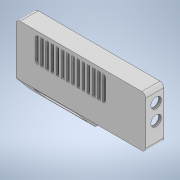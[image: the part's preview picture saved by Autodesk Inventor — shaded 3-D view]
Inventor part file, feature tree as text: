
AUTODESK INVENTOR PART (.ipt)
format: ipt  version: 2021 (Build 250183000, 183)  size: 544,768 bytes
history: native  units: mm
features: sketch x22, extrude x21, chamfer x6, fillet x4, hole x1
ambient origin geometry x8: Origin, YZ Plane, XZ Plane, XY Plane, X Axis, Y Axis, Z Axis, Center Point
bodies: Solid1 (feature_tree)
feature tree (54):
  extrude  "Extrusion1"  Depth=100.0mm
  extrude  "Extrusion3"  Depth=50.0mm
  extrude  "Extrusion4"  Depth=12.5mm
  extrude  "Extrusion12"  Depth=3.0mm TaperAngle=0.0deg
  extrude  "Extrusion13"  Depth=3.0mm TaperAngle=0.0deg
  fillet  "Fillet3"  Radius=2.0mm
  extrude  "Extrusion15"  Depth=2.0mm
  extrude  "Extrusion20"  Depth=1.2mm
  extrude  "Extrusion21"  Depth=12.0mm TaperAngle=0.0deg
  extrude  "Extrusion22"  Depth=2.0mm
  extrude  "Extrusion23"  Depth=3.0mm
  extrude  "Extrusion26"  Depth=4.4mm TaperAngle=0.0deg
  hole  "Hole2"  [1 undecoded]
  chamfer  "Chamfer3"  Distance=12.0mm
  chamfer  "Chamfer4"  Distance=12.0mm
  chamfer  "Chamfer5"  Distance=2.0mm
  chamfer  "Chamfer6"  Distance=2.0mm
  chamfer  "Chamfer7"  Distance=3.0mm
  extrude  "Extrusion27"  Depth=3.0mm
  fillet  "Fillet4"  Radius=3.0mm
  extrude  "Extrusion28"  Depth=50.0mm
  extrude  "Extrusion29"  Depth=0.5mm
  extrude  "Extrusion30"  Depth=15.0mm
  fillet  "Fillet5"  Radius=3.0mm
  extrude  "Extrusion34"  Depth=3.0mm
  extrude  "Extrusion35"  Depth=0.5mm
  extrude  "Extrusion36"  Depth=0.5mm
  extrude  "Extrusion37"  Depth=0.5mm
  fillet  "Fillet6"  Radius=4.8mm
  extrude  "Extrusion38"  Depth=0.5mm
  extrude  "Extrusion39"  Depth=0.5mm
  chamfer  "Chamfer8"  Distance=4.8mm
  sketch  "Sketch1"  dims[d0=52.0mm d1=100.0mm]
  sketch  "Sketch4"  dims[d2=26.0mm d3=50.0mm]
  sketch  "Sketch5"  dims[d4=2.0mm d5=0.0mm d35=12.5mm]
  sketch  "Sketch13"  dims[d36=63.1mm d37=3.0mm d38=0.0mm]
  sketch  "Sketch14"  dims[d39=50.673mm d40=3.0mm d41=0.0mm d79=2.0mm]
  sketch  "Sketch16"  dims[d80=2.0mm d81=2.0mm]
  sketch  "Sketch21"  dims[d82=1.2mm d83=44.0mm]
  sketch  "Sketch22"  dims[d84=59.0mm d85=12.0mm d86=0.0mm]
  sketch  "Sketch23"  dims[d87=2.0mm d88=12.6mm]
  sketch  "Sketch24"  dims[d89=12.0mm d90=0.0mm d91=3.0mm]
  sketch  "Sketch27"  dims[d95=33.8mm d96=4.4mm d97=0.0mm]
  sketch  "Sketch28"  dims[d117=2.0mm d118=2.0mm d119=12.0mm d120=0.0mm d121=12.0mm d122=0.0mm]
  sketch  "Sketch29"  dims[d123=70.0mm]
  sketch  "Sketch30"  dims[d124=89.0mm]
  sketch  "Sketch31"  dims[d125=8.0mm]
  sketch  "Sketch32"  dims[d126=8.0mm d127=2.0mm d128=0.0mm]
  sketch  "Sketch36"  dims[d129=8.0mm]
  sketch  "Sketch37"  dims[d130=10.0mm]
  sketch  "Sketch38"  dims[d131=12.0mm]
  sketch  "Sketch39"  dims[d132=8.0mm]
  sketch  "Sketch40"  dims[d133=8.0mm]
  sketch  "Sketch41"  dims[d134=8.0mm d135=2.0mm d136=0.0mm d144=3.0mm d145=3.0mm d146=3.0mm d147=50.0mm d148=97.0mm d149=15.0mm d150=3.0mm d151=3.0mm d152=97.0mm d153=49.0mm d154=4.8mm d155=4.8mm d156=4.8mm d157=4.8mm d158=4.8mm d159=5.0mm d160=0.0mm d161=2.0mm d162=6.0mm d163=4.0mm d164=2.0mm d165=90.0deg d166=4.0mm d167=20.594885mm d168=2.0mm d169=2.0mm d170=45.0deg d171=1.0mm d172=2.0mm d173=45.0deg d174=2.0mm d175=2.0mm d176=45.0deg d177=2.0mm d178=2.0mm d179=45.0deg d180=0.8mm d181=2.0mm d182=45.0deg d184=68.0mm d189=2.0mm d190=0.0mm d191=2.0mm d192=2.0mm d193=24.0mm d194=2.0mm d195=0.0mm d196=36.5mm d197=46.5mm d198=3.5mm d199=2.0mm d200=0.0mm d201=12.5mm d202=23.0mm d203=3.5mm d204=2.0mm d205=0.0mm d206=1.0mm d217=7.6mm d218=10.0mm d219=46.4mm d220=20.0mm d221=0.0mm d222=22.68928mm d223=67.0mm d224=0.0mm d225=1.2mm d226=0.0mm d227=1.2mm d228=0.0mm d229=3.0mm d230=12.3mm d231=33.2mm d232=1.0mm d233=10.0mm d234=1.2mm d235=0.0mm d236=1.2mm d237=5.0mm d238=20.0mm d239=1.5mm d240=0.0mm d241=1.5mm d242=2.0mm d243=45.0deg d67=0.5mm d68=0.872665mm d69=0.5mm d70=0.872665mm d71=0.5mm d72=0.872665mm d73=0.5mm d74=0.872665mm d75=0.872665mm d76=0.5mm d77=0.872665mm d208=0.5mm d209=0.872665mm d210=0.5mm d211=0.872665mm]
note: 1 required parameter value undecoded (feature->parameter linkage not recoverable at this tier; creation-order binding heuristic only, values carry confidence <= 0.55)
